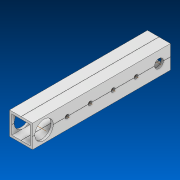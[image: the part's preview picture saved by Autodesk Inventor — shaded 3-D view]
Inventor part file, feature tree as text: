
AUTODESK INVENTOR PART (.ipt)
format: ipt  version: 2022.2 (Build 262287000, 287)  size: 704,512 bytes
history: native  units: in
note: dims shown in document units (in); Inventor stores cm internally (conversion verified against a paired STEP export)
features: other x6, extrude x2, pattern_linear x1, sketch x1, pattern_circular x1
ambient origin geometry x8: Origin, YZ Plane, XZ Plane, XY Plane, X Axis, Y Axis, Z Axis, Center Point
bodies: Solid1 (feature_tree)
feature tree (11):
  extrude  "Extrusion1"  Depth=0.8in
  other  "Work Axis1"
  pattern_linear  "Rectangular Pattern1"  Spacing1=0.0in  [1 undecoded]
  extrude  "Extrusion2"  Depth=0.8in
  sketch  "Sketch1"  dims[d0=1.0in d1=53.0in d2=0.0in d3=2.3622in d5=1.0in d7=0.0in d8=0.0in d9=0.8in]
  other  "Work Axis2"
  other  "Work Axis3"
  other  "Work Axis4"
  other  "Work Axis5"
  other  "Work Axis6"
  pattern_circular  "CirPattern2"
note: 1 required parameter value undecoded (feature->parameter linkage not recoverable at this tier; creation-order binding heuristic only, values carry confidence <= 0.55)
